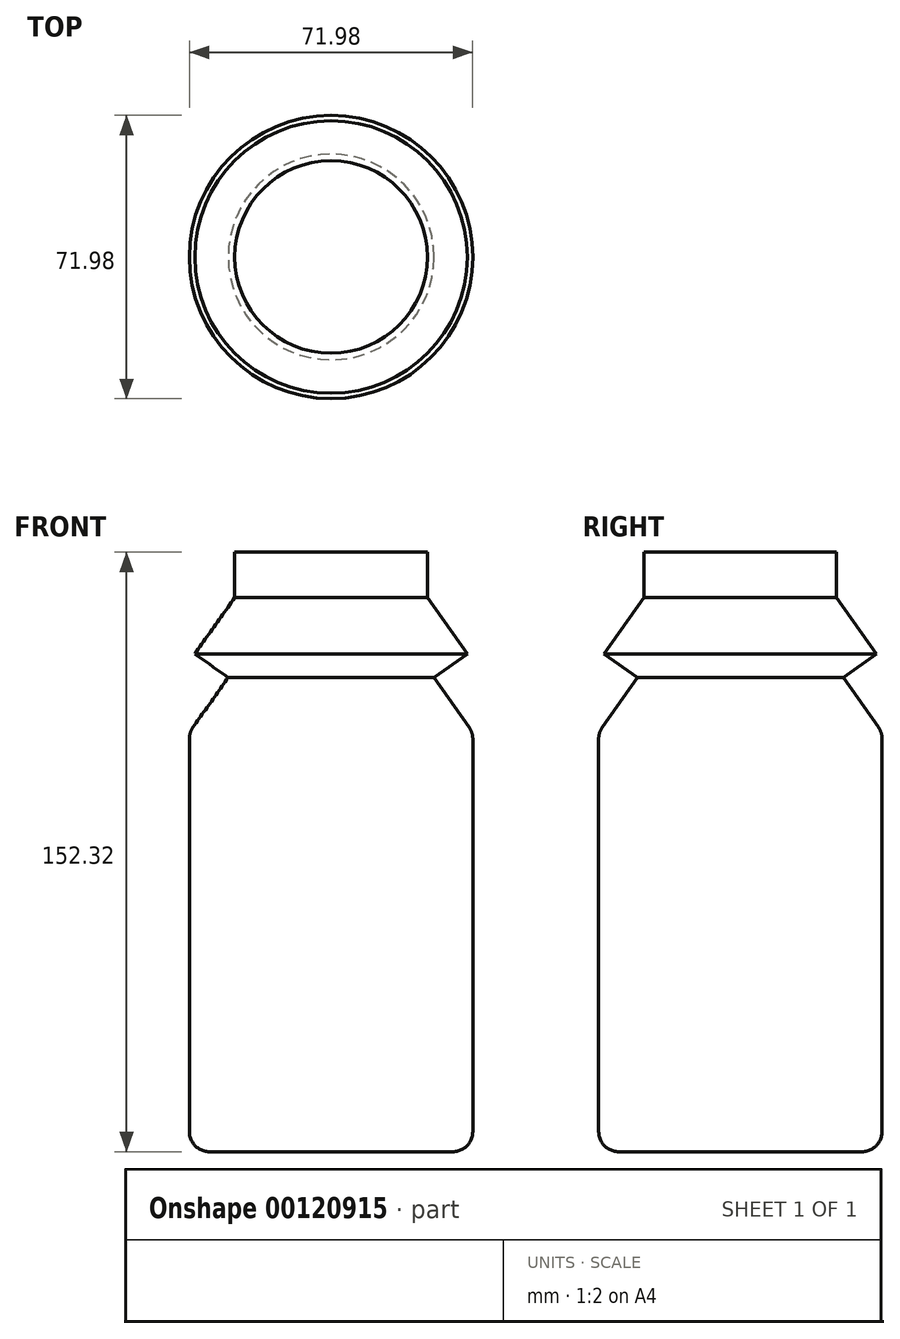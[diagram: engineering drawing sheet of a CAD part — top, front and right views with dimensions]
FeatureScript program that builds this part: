
annotation { "Feature Type Name" : "Feature", "Feature Type Description" : "" }
export const myFeature = defineFeature(function(context is Context, id is Id, definition is map)
    precondition{}
    {
        {
            var Q0;
            Q0=qCreatedBy(makeId("Front.planeOp"),FACE);
            var sketch = newSketch(context, id + "F0", { "sketchPlane" : qUnion([Q0])});
            skLineSegment(sketch, "E0", {"start": v(0, 76.4) * mm, "end": v(24.46, 76.4) * mm});
            skLineSegment(sketch, "E1", {"start": v(24.46, 76.4) * mm, "end": v(24.46, 64.85) * mm});
            skLineSegment(sketch, "E2", {"start": v(24.46, 64.85) * mm, "end": v(34.62, 50.54) * mm});
            skLineSegment(sketch, "E3", {"start": v(34.62, 50.54) * mm, "end": v(26.13, 44.52) * mm});
            skLineSegment(sketch, "E4", {"start": v(26.13, 44.52) * mm, "end": v(36, 30.63) * mm});
            skLineSegment(sketch, "E5", {"start": v(36, 30.63) * mm, "end": v(36, -75.93) * mm});
            skLineSegment(sketch, "E6", {"start": v(36, -75.93) * mm, "end": v(0, -75.93) * mm});
            skLineSegment(sketch, "E7", {"start": v(0, -75.93) * mm, "end": v(0, 76.4) * mm});
            skSolve(sketch);
        }
        {
            var Q0;
            Q0 = qSketchRegion(id + "F0", true);
            var Q1;
            Q1=sQuery(id+"F0.wireOp",EDGE,"E7");
            revolve(context, id + "F1", {"entities" : qUnion([Q0]), "axis" : qUnion([Q1]), "revolveType" : RevolveType.FULL});
        }
        {
            var Q0;
            Q0=makeQuery(id+"F1.opRevolve","SWEPT_FACE",FACE,{"disambiguationData":[OSD([sQuery(id+"F0.wireOp",EDGE,"E5")])]});
            fillet(context, id + "F2", {"entities" : qUnion([Q0]), "radius" : 5.08 * mm, "tangentPropagation" : true, "allowEdgeOverflow" : false});
        }
    });
